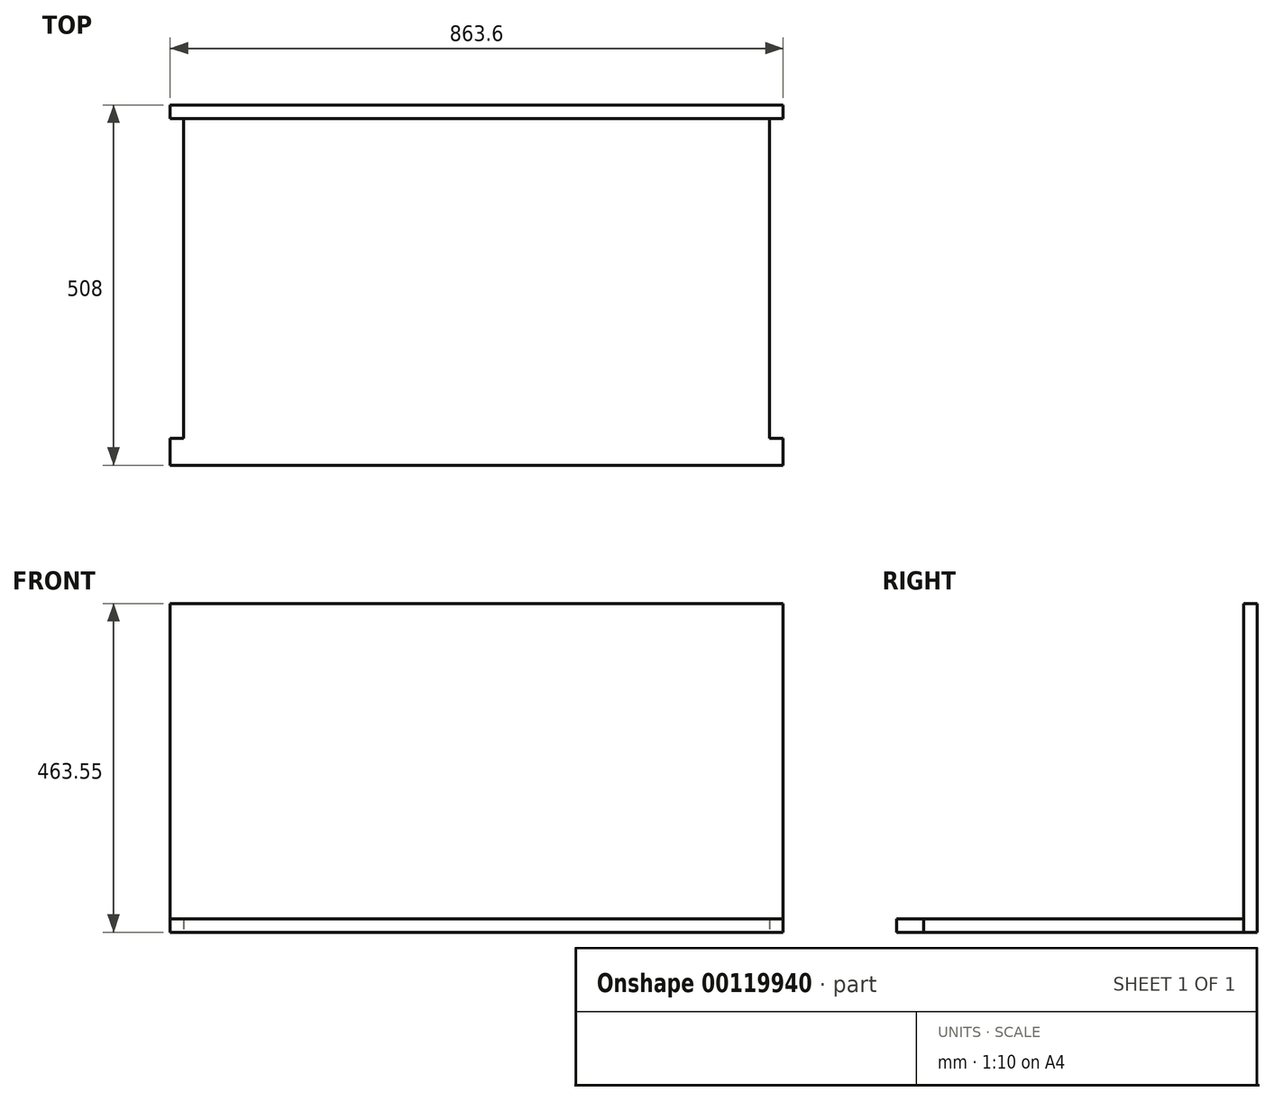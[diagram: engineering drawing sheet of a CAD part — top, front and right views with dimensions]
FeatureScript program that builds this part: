
annotation { "Feature Type Name" : "Feature", "Feature Type Description" : "" }
export const myFeature = defineFeature(function(context is Context, id is Id, definition is map)
    precondition{}
    {
        {
            var Q0;
            Q0=qCreatedBy(makeId("Top.planeOp"),FACE);
            var sketch = newSketch(context, id + "F0", { "sketchPlane" : qUnion([Q0])});
            skLineSegment(sketch, "E0.bottom", {"start": v(0, 0) * mm, "end": v(863.6, 0) * mm});
            skLineSegment(sketch, "E0.top", {"start": v(0, 508) * mm, "end": v(863.6, 508) * mm});
            skLineSegment(sketch, "E0.left", {"start": v(0, 0) * mm, "end": v(0, 508) * mm});
            skLineSegment(sketch, "E0.right", {"start": v(863.6, 0) * mm, "end": v(863.6, 508) * mm});
            skLineSegment(sketch, "E1", {"start": v(0, 488.95) * mm, "end": v(863.6, 488.95) * mm});
            skLineSegment(sketch, "E2.bottom", {"start": v(0, 488.95) * mm, "end": v(19.05, 488.95) * mm});
            skLineSegment(sketch, "E2.top", {"start": v(0, 38.1) * mm, "end": v(19.05, 38.1) * mm});
            skLineSegment(sketch, "E2.left", {"start": v(0, 488.95) * mm, "end": v(0, 38.1) * mm});
            skLineSegment(sketch, "E2.right", {"start": v(19.05, 488.95) * mm, "end": v(19.05, 38.1) * mm});
            skLineSegment(sketch, "E3.bottom", {"start": v(863.6, 488.95) * mm, "end": v(844.55, 488.95) * mm});
            skLineSegment(sketch, "E3.top", {"start": v(863.6, 38.1) * mm, "end": v(844.55, 38.1) * mm});
            skLineSegment(sketch, "E3.left", {"start": v(863.6, 488.95) * mm, "end": v(863.6, 38.1) * mm});
            skLineSegment(sketch, "E3.right", {"start": v(844.55, 488.95) * mm, "end": v(844.55, 38.1) * mm});
            skSolve(sketch);
        }
        {
            var Q0;
            Q0=makeQuery(id+"F0.imprint","IMPRINT",FACE,{"disambiguationData":[TD([[makeQuery(id+"F0.imprint","IMPRINT",EDGE,{"derivedFrom":sQuery(id+"F0.wireOp",EDGE,"E2.bottom")}),-1.0]])]});
            var Q1;
            {var subQ1=sQuery(id+"F0.wireOp",EDGE,"E0.top");Q1=makeQuery(id+"F0.imprint","IMPRINT",FACE,{"disambiguationData":[TD([[makeQuery(id+"F0.imprint","IMPRINT",EDGE,{"derivedFrom":subQ1}),-1.0]])]});}
            var Q2;
            Q2=makeQuery(id+"F0.imprint","IMPRINT",FACE,{"disambiguationData":[TD([[makeQuery(id+"F0.imprint","IMPRINT",EDGE,{"derivedFrom":sQuery(id+"F0.wireOp",EDGE,"E3.bottom")}),1.0]])]});
            extrude(context, id + "F1", {"entities" : qUnion([Q0, Q1, Q2]), "depth" : 463.55 * mm});
        }
        {
            var Q0;
            {var subQ1=sQuery(id+"F0.wireOp",EDGE,"E0.bottom");Q0=makeQuery(id+"F0.imprint","IMPRINT",FACE,{"disambiguationData":[TD([[makeQuery(id+"F0.imprint","IMPRINT",EDGE,{"derivedFrom":subQ1}),1.0]])]});}
            extrude(context, id + "F2", {"entities" : qUnion([Q0]), "operationType" : NewBodyOperationType.ADD, "depth" : 19.05 * mm});
        }
    });
